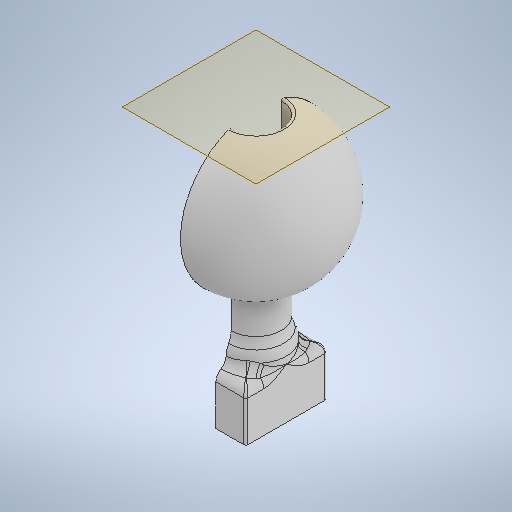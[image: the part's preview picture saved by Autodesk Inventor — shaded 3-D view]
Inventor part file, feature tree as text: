
AUTODESK INVENTOR PART (.ipt)
format: ipt  version: 2025.1 (Build 291241000, 241)  size: 491,008 bytes
history: native  units: mm
features: sketch x6, extrude x5, fillet x5, revolve x1, plane x1
ambient origin geometry x8: Origin, YZ Plane, XZ Plane, XY Plane, X Axis, Y Axis, Z Axis, Center Point
bodies: Volumenkörper1 (feature_tree)
feature tree (18):
  extrude  "Extrusion1"  Depth=2.0mm TaperAngle=0.0deg
  extrude  "Extrusion2"  Depth=4.0mm TaperAngle=0.0deg
  revolve  "Umdrehung1"
  plane  "Arbeitsebene1"
  extrude  "Extrusion3"  Depth=7.5mm
  extrude  "Extrusion5"  Depth=13.0mm
  extrude  "Extrusion4"  TaperAngle=90.0deg  [1 undecoded]
  fillet  "Rundung1"  Radius=5.0mm
  fillet  "Rundung2"  Radius=10.0mm
  fillet  "Rundung3"  Radius=3.3mm
  fillet  "Rundung4"  Radius=25.0mm
  fillet  "Rundung5"  Radius=2.0mm
  sketch  "Skizze1"  dims[d0=6.0mm d1=2.0mm d2=0.0mm]
  sketch  "Skizze2"  dims[d3=5.0mm d4=4.0mm d5=0.0mm]
  sketch  "Skizze3"  dims[d6=15.0mm d7=7.5mm]
  sketch  "Skizze4"  dims[d8=7.5mm d10=13.0mm]
  sketch  "Skizze5"  dims[d11=0.0mm d12=90.0deg d13=5.0mm d14=10.0mm d15=0.0mm d16=3.3mm d17=25.0mm d18=0.0mm d19=2.0mm]
  sketch  "Skizze6"  dims[d20=0.2mm d21=4.0mm d22=4.0mm d23=6.0mm d24=3.0mm d25=5.0mm d26=0.0mm d27=0.2mm d28=1.0mm d29=1.0mm]
note: 1 required parameter value undecoded (feature->parameter linkage not recoverable at this tier; creation-order binding heuristic only, values carry confidence <= 0.55)
